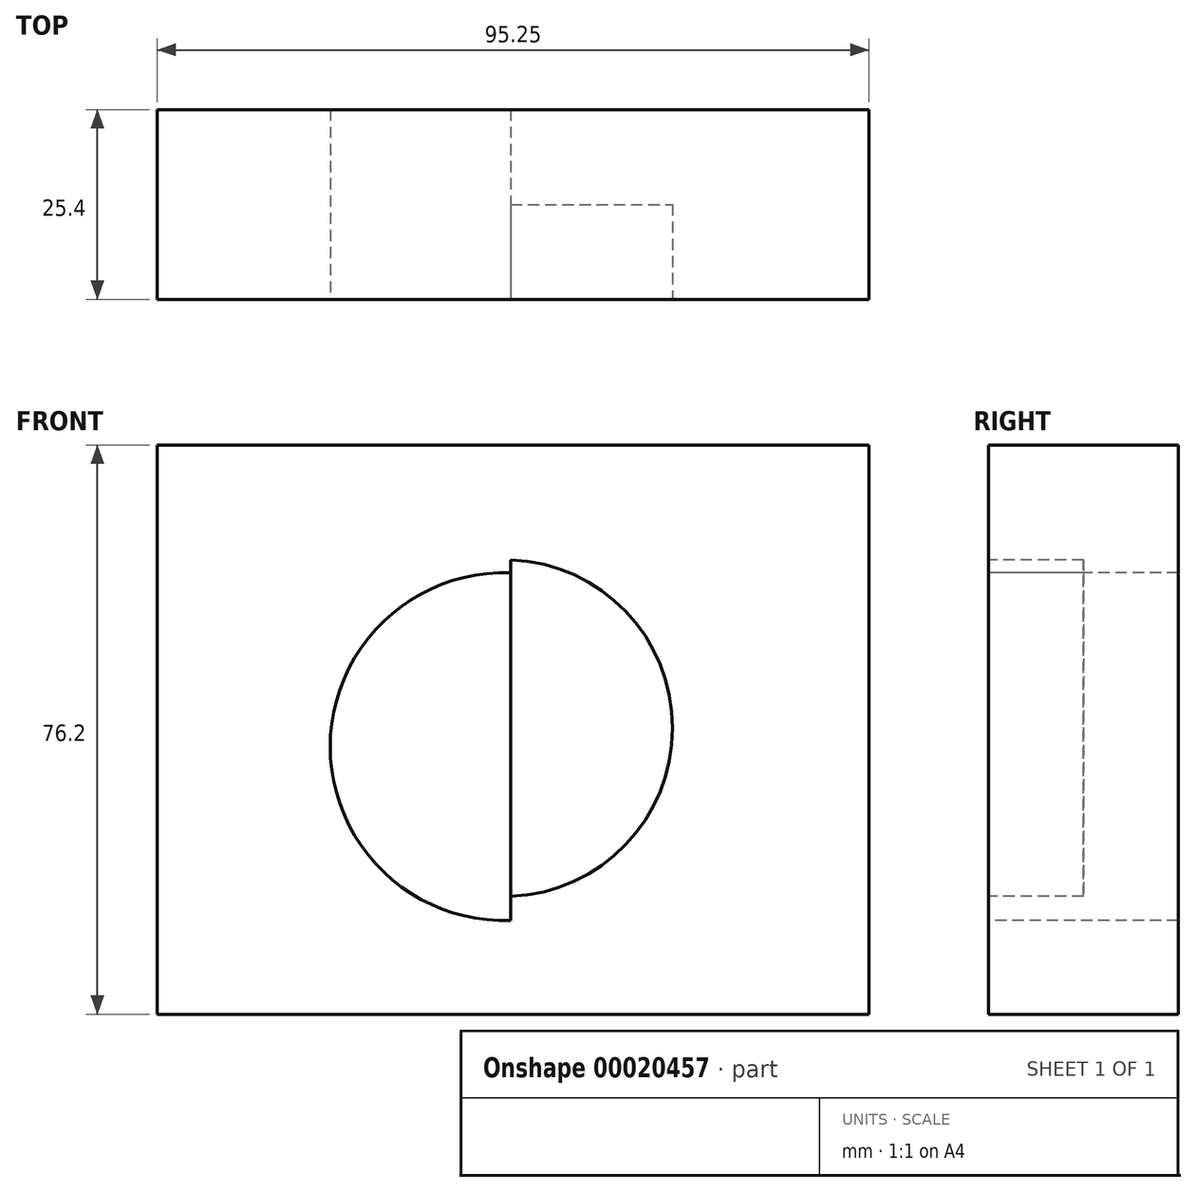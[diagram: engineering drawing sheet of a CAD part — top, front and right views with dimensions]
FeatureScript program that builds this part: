
annotation { "Feature Type Name" : "Feature", "Feature Type Description" : "" }
export const myFeature = defineFeature(function(context is Context, id is Id, definition is map)
    precondition{}
    {
        {
            var Q0;
            Q0=qCreatedBy(makeId("Front.planeOp"),FACE);
            var sketch = newSketch(context, id + "F0", { "sketchPlane" : qUnion([Q0])});
            skLineSegment(sketch, "E0.bottom", {"start": v(-46.43, 29.83) * mm, "end": v(48.82, 29.83) * mm});
            skLineSegment(sketch, "E0.top", {"start": v(-46.43, -46.37) * mm, "end": v(48.82, -46.37) * mm});
            skLineSegment(sketch, "E0.left", {"start": v(-46.43, 29.83) * mm, "end": v(-46.43, -46.37) * mm});
            skLineSegment(sketch, "E0.right", {"start": v(48.82, 29.83) * mm, "end": v(48.82, -46.37) * mm});
            skSolve(sketch);
        }
        {
            var Q0;
            Q0 = qSketchRegion(id + "F0", true);
            extrude(context, id + "F1", {"entities" : qUnion([Q0]), "depth" : 25.4 * mm});
        }
        {
            var Q0;
            Q0=makeQuery(id+"F1.opExtrude","CAP_FACE",FACE,{"disambiguationData":[OSD([sQuery(id+"F0.wireOp",EDGE,"E0.bottom"),sQuery(id+"F0.wireOp",EDGE,"E0.top"),sQuery(id+"F0.wireOp",EDGE,"E0.left"),sQuery(id+"F0.wireOp",EDGE,"E0.right")])],"isStart":false});
            var sketch = newSketch(context, id + "F2", { "sketchPlane" : qUnion([Q0])});
            skLineSegment(sketch, "E1.0", {"start": v(0.9, 29.83) * mm, "end": v(0.9, -46.37) * mm});
            skSolve(sketch);
        }
        {
            var Q0;
            {var subQ1=sQuery(id+"F2.wireOp",EDGE,"E1.0");Q0=makeQuery(id+"F2.imprint","IMPRINT",FACE,{"disambiguationData":[TD([[makeQuery(id+"F2.imprint","IMPRINT",EDGE,{"derivedFrom":subQ1}),-1.0]])]});}
            var sketch = newSketch(context, id + "F3", { "sketchPlane" : qUnion([Q0])});
            skCircle(sketch, "E2", {"center": v(0, -8.07) * mm, "radius": 22.54 * mm});
            skSolve(sketch);
        }
        {
            var Q0;
            {var subQ0=makeQuery(id+"F2.imprint","IMPRINT",EDGE,{"derivedFrom":sQuery(id+"F2.wireOp",EDGE,"E1.0")});var subQ1=sQuery(id+"F3.wireOp",EDGE,"E2");var subQ3=makeQuery(id+"F3.imprint","INTERSECT",VERTEX,{"disambiguationData":[OD(0.0)],"derivedFrom":[subQ0,subQ1]});Q0=makeQuery(id+"F3.imprint","IMPRINT",FACE,{"disambiguationData":[TD([[makeQuery(id+"F3.imprint","IMPRINT",EDGE,{"disambiguationData":[TD([[subQ3,1.0]])],"derivedFrom":subQ1}),1.0]])]});}
            extrude(context, id + "F4", {"entities" : qUnion([Q0]), "operationType" : NewBodyOperationType.REMOVE, "endBound" : BoundingType.SYMMETRIC, "oppositeDirection" : true, "depth" : 25.4 * mm});
        }
        {
            var Q0;
            {var subQ1=sQuery(id+"F2.wireOp",EDGE,"E1.0");Q0=makeQuery(id+"F2.imprint","IMPRINT",FACE,{"disambiguationData":[TD([[makeQuery(id+"F2.imprint","IMPRINT",EDGE,{"derivedFrom":subQ1}),-1.0]])]});}
            var sketch = newSketch(context, id + "F5", { "sketchPlane" : qUnion([Q0])});
            skCircle(sketch, "E3", {"center": v(0, -10.56) * mm, "radius": 23.27 * mm});
            skSolve(sketch);
        }
        {
            var Q0;
            {var subQ0=makeQuery(id+"F2.imprint","IMPRINT",EDGE,{"derivedFrom":sQuery(id+"F2.wireOp",EDGE,"E1.0")});var subQ1=sQuery(id+"F5.wireOp",EDGE,"E3");var subQ3=makeQuery(id+"F5.imprint","INTERSECT",VERTEX,{"disambiguationData":[OD(0.0)],"derivedFrom":[subQ0,subQ1]});Q0=makeQuery(id+"F5.imprint","IMPRINT",FACE,{"disambiguationData":[TD([[makeQuery(id+"F5.imprint","IMPRINT",EDGE,{"disambiguationData":[TD([[subQ3,-1.0]])],"derivedFrom":subQ1}),1.0]])]});}
            extrude(context, id + "F6", {"entities" : qUnion([Q0]), "operationType" : NewBodyOperationType.REMOVE, "oppositeDirection" : true, "depth" : 25.4 * mm});
        }
    });
